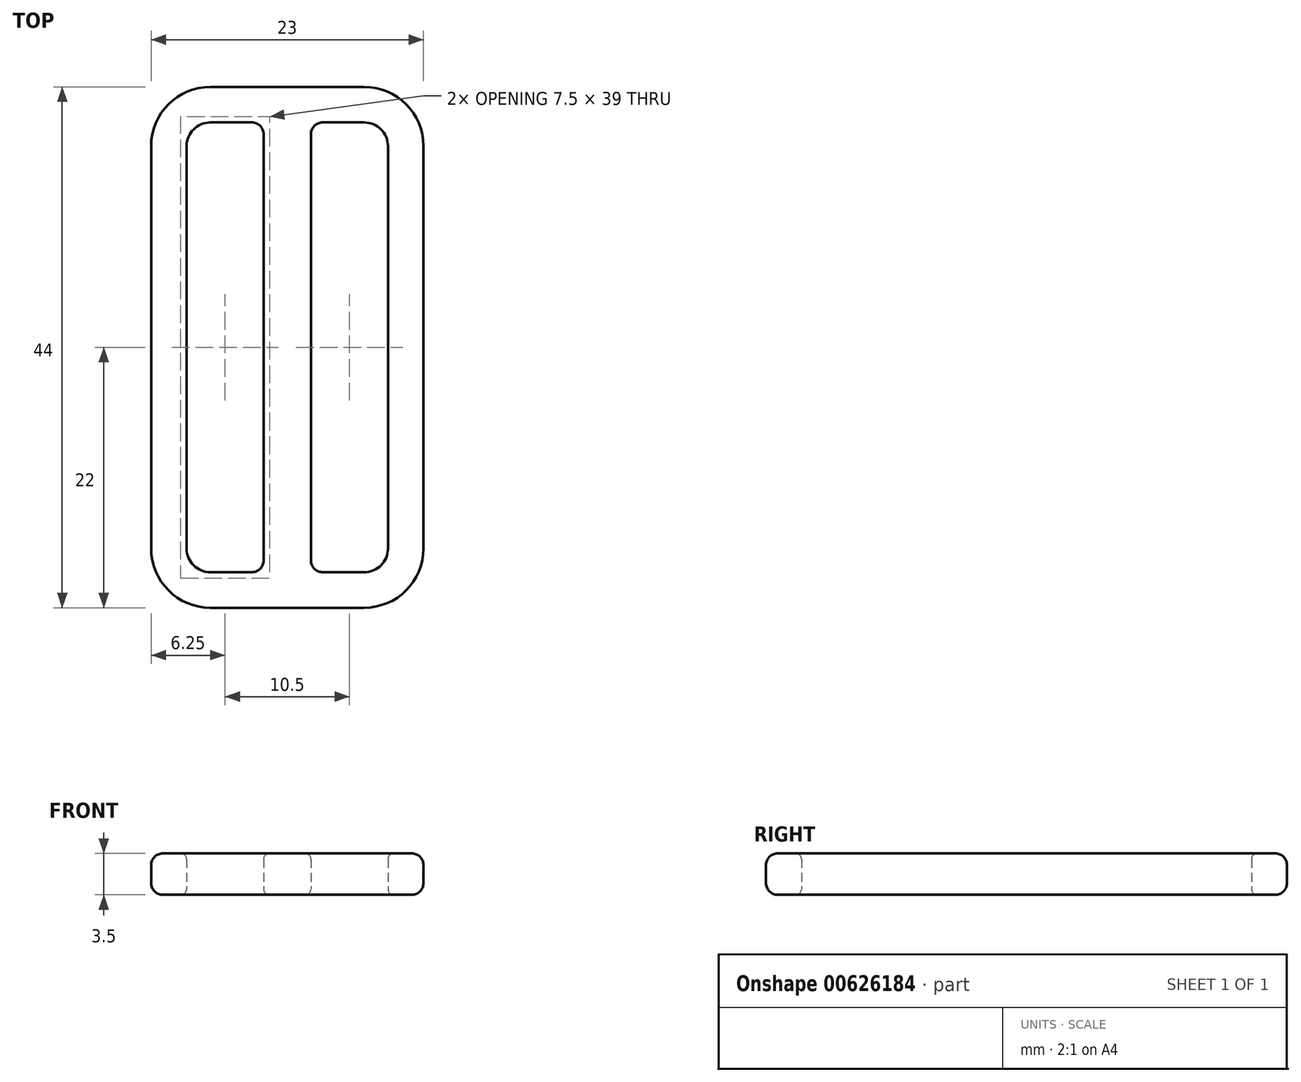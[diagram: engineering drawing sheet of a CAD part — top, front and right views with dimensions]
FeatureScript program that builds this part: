
annotation { "Feature Type Name" : "Feature", "Feature Type Description" : "" }
export const myFeature = defineFeature(function(context is Context, id is Id, definition is map)
    precondition{}
    {
        {
            var Q0;
            Q0=qCreatedBy(makeId("Top.planeOp"),FACE);
            var sketch = newSketch(context, id + "F0", { "sketchPlane" : qUnion([Q0])});
            skLineSegment(sketch, "E0.bottom", {"start": v(-8.5, 19) * mm, "end": v(-2, 19) * mm});
            skLineSegment(sketch, "E0.top", {"start": v(-8.5, -19) * mm, "end": v(-2, -19) * mm});
            skLineSegment(sketch, "E0.left", {"start": v(-8.5, 19) * mm, "end": v(-8.5, -19) * mm});
            skLineSegment(sketch, "E0.right", {"start": v(-2, 19) * mm, "end": v(-2, -19) * mm});
            skLineSegment(sketch, "E1.bottom", {"start": v(2, 19) * mm, "end": v(8.5, 19) * mm});
            skLineSegment(sketch, "E1.top", {"start": v(2, -19) * mm, "end": v(8.5, -19) * mm});
            skLineSegment(sketch, "E1.left", {"start": v(8.5, 19) * mm, "end": v(8.5, -19) * mm});
            skLineSegment(sketch, "E1.right", {"start": v(2, 19) * mm, "end": v(2, -19) * mm});
            skLineSegment(sketch, "E2", {"start": v(-2, 0) * mm, "end": v(2, 0) * mm, "construction": true});
            skPoint(sketch, "E3", {"position": v(0, 0) * mm});
            skLineSegment(sketch, "E4.bottom", {"start": v(-6.5, 22) * mm, "end": v(6.5, 22) * mm});
            skLineSegment(sketch, "E4.top", {"start": v(-6.5, -22) * mm, "end": v(6.5, -22) * mm});
            skLineSegment(sketch, "E4.left", {"start": v(-11.5, 17) * mm, "end": v(-11.5, -17) * mm});
            skLineSegment(sketch, "E4.right", {"start": v(11.5, 17) * mm, "end": v(11.5, -17) * mm});
            skPoint(sketch, "E5.visualSharp", {"position": v(-11.5, 22) * mm});
            skArc(sketch, "E5.filletArc", {"start": v(-6.5, 22) * mm, "mid": v(-10.04, 20.54) * mm, "end": v(-11.5, 17) * mm});
            skPoint(sketch, "E6.visualSharp", {"position": v(11.5, 22) * mm});
            skArc(sketch, "E6.filletArc", {"start": v(11.5, 17) * mm, "mid": v(10.04, 20.54) * mm, "end": v(6.5, 22) * mm});
            skPoint(sketch, "E7.visualSharp", {"position": v(11.5, -22) * mm});
            skArc(sketch, "E7.filletArc", {"start": v(6.5, -22) * mm, "mid": v(10.04, -20.54) * mm, "end": v(11.5, -17) * mm});
            skPoint(sketch, "E8.visualSharp", {"position": v(-11.5, -22) * mm});
            skArc(sketch, "E8.filletArc", {"start": v(-11.5, -17) * mm, "mid": v(-10.04, -20.54) * mm, "end": v(-6.5, -22) * mm});
            skSolve(sketch);
        }
        {
            var Q0;
            Q0=makeQuery(id+"F0.imprint","IMPRINT",FACE,{"disambiguationData":[TD([[makeQuery(id+"F0.imprint","IMPRINT",EDGE,{"derivedFrom":sQuery(id+"F0.wireOp",EDGE,"E0.bottom")}),1.0]])]});
            extrude(context, id + "F1", {"entities" : qUnion([Q0]), "depth" : 3.5 * mm, "offsetDistance" : 25 * mm});
        }
        {
            var Q0;
            Q0=makeQuery(id+"F1.opExtrude","SWEPT_EDGE",EDGE,{"disambiguationData":[OSD([sQuery(id+"F0.wireOp",EDGE,"E0.bottom"),sQuery(id+"F0.wireOp",EDGE,"E0.left")])]});
            var Q1;
            Q1=makeQuery(id+"F1.opExtrude","SWEPT_EDGE",EDGE,{"disambiguationData":[OSD([sQuery(id+"F0.wireOp",EDGE,"E1.top"),sQuery(id+"F0.wireOp",EDGE,"E1.left")])]});
            var Q2;
            Q2=makeQuery(id+"F1.opExtrude","SWEPT_EDGE",EDGE,{"disambiguationData":[OSD([sQuery(id+"F0.wireOp",EDGE,"E1.bottom"),sQuery(id+"F0.wireOp",EDGE,"E1.left")])]});
            var Q3;
            Q3=makeQuery(id+"F1.opExtrude","SWEPT_EDGE",EDGE,{"disambiguationData":[OSD([sQuery(id+"F0.wireOp",EDGE,"E0.top"),sQuery(id+"F0.wireOp",EDGE,"E0.left")])]});
            fillet(context, id + "F2", {"entities" : qUnion([Q0, Q1, Q2, Q3]), "radius" : 2 * mm, "tangentPropagation" : true, "allowEdgeOverflow" : false});
        }
        {
            var Q0;
            Q0=makeQuery(id+"F1.opExtrude","SWEPT_EDGE",EDGE,{"disambiguationData":[OSD([sQuery(id+"F0.wireOp",EDGE,"E1.bottom"),sQuery(id+"F0.wireOp",EDGE,"E1.right")])]});
            var Q1;
            Q1=makeQuery(id+"F1.opExtrude","SWEPT_EDGE",EDGE,{"disambiguationData":[OSD([sQuery(id+"F0.wireOp",EDGE,"E0.bottom"),sQuery(id+"F0.wireOp",EDGE,"E0.right")])]});
            var Q2;
            Q2=makeQuery(id+"F1.opExtrude","SWEPT_EDGE",EDGE,{"disambiguationData":[OSD([sQuery(id+"F0.wireOp",EDGE,"E0.top"),sQuery(id+"F0.wireOp",EDGE,"E0.right")])]});
            var Q3;
            Q3=makeQuery(id+"F1.opExtrude","SWEPT_EDGE",EDGE,{"disambiguationData":[OSD([sQuery(id+"F0.wireOp",EDGE,"E1.top"),sQuery(id+"F0.wireOp",EDGE,"E1.right")])]});
            fillet(context, id + "F3", {"entities" : qUnion([Q0, Q1, Q2, Q3]), "radius" : 1 * mm, "tangentPropagation" : true, "allowEdgeOverflow" : false});
        }
        {
            var Q0;
            Q0=makeQuery(id+"F1.opExtrude","CAP_EDGE",EDGE,{"disambiguationData":[OSD([sQuery(id+"F0.wireOp",EDGE,"E4.left")])],"isStart":false});
            var Q1;
            {var subQ0=sQuery(id+"F0.wireOp",EDGE,"E1.right");var subQ1=sQuery(id+"F0.wireOp",EDGE,"E1.bottom");Q1=makeQuery(id+"F2.opFillet","BLEND_EDGE",EDGE,{"blendedFrom":[makeQuery(id+"F1.opExtrude","SWEPT_EDGE",EDGE,{"disambiguationData":[OSD([subQ1,subQ0])]}),makeQuery(id+"F1.opExtrude","CAP_FACE",FACE,{"disambiguationData":[OSD([sQuery(id+"F0.wireOp",EDGE,"E0.bottom"),sQuery(id+"F0.wireOp",EDGE,"E0.top"),sQuery(id+"F0.wireOp",EDGE,"E0.left"),sQuery(id+"F0.wireOp",EDGE,"E0.right"),subQ1,sQuery(id+"F0.wireOp",EDGE,"E1.top"),sQuery(id+"F0.wireOp",EDGE,"E1.left"),subQ0,sQuery(id+"F0.wireOp",EDGE,"E4.bottom"),sQuery(id+"F0.wireOp",EDGE,"E4.top"),sQuery(id+"F0.wireOp",EDGE,"E4.left"),sQuery(id+"F0.wireOp",EDGE,"E4.right"),sQuery(id+"F0.wireOp",EDGE,"E5.filletArc"),sQuery(id+"F0.wireOp",EDGE,"E6.filletArc"),sQuery(id+"F0.wireOp",EDGE,"E7.filletArc"),sQuery(id+"F0.wireOp",EDGE,"E8.filletArc")])],"isStart":true})],"blendedInto":[makeQuery(id+"F1.opExtrude","CAP_FACE",FACE,{"disambiguationData":[OSD([sQuery(id+"F0.wireOp",EDGE,"E0.bottom"),sQuery(id+"F0.wireOp",EDGE,"E0.top"),sQuery(id+"F0.wireOp",EDGE,"E0.left"),sQuery(id+"F0.wireOp",EDGE,"E0.right"),subQ1,sQuery(id+"F0.wireOp",EDGE,"E1.top"),sQuery(id+"F0.wireOp",EDGE,"E1.left"),subQ0,sQuery(id+"F0.wireOp",EDGE,"E4.bottom"),sQuery(id+"F0.wireOp",EDGE,"E4.top"),sQuery(id+"F0.wireOp",EDGE,"E4.left"),sQuery(id+"F0.wireOp",EDGE,"E4.right"),sQuery(id+"F0.wireOp",EDGE,"E5.filletArc"),sQuery(id+"F0.wireOp",EDGE,"E6.filletArc"),sQuery(id+"F0.wireOp",EDGE,"E7.filletArc"),sQuery(id+"F0.wireOp",EDGE,"E8.filletArc")])],"isStart":true})]});}
            var Q2;
            Q2=makeQuery(id+"F1.opExtrude","CAP_EDGE",EDGE,{"disambiguationData":[OSD([sQuery(id+"F0.wireOp",EDGE,"E4.right")])],"isStart":true});
            fillet(context, id + "F4", {"entities" : qUnion([Q0, Q1, Q2]), "radius" : 1 * mm, "tangentPropagation" : true, "allowEdgeOverflow" : false});
        }
        {
            var Q0;
            Q0=makeQuery(id+"F1.opExtrude","CAP_EDGE",EDGE,{"disambiguationData":[OSD([sQuery(id+"F0.wireOp",EDGE,"E1.top")])],"isStart":false});
            var Q1;
            {var subQ0=sQuery(id+"F0.wireOp",EDGE,"E0.right");var subQ1=sQuery(id+"F0.wireOp",EDGE,"E0.top");Q1=makeQuery(id+"F3.opFillet","BLEND_EDGE",EDGE,{"blendedFrom":[makeQuery(id+"F1.opExtrude","SWEPT_EDGE",EDGE,{"disambiguationData":[OSD([subQ1,subQ0])]}),makeQuery(id+"F1.opExtrude","CAP_FACE",FACE,{"disambiguationData":[OSD([sQuery(id+"F0.wireOp",EDGE,"E0.bottom"),subQ1,sQuery(id+"F0.wireOp",EDGE,"E0.left"),subQ0,sQuery(id+"F0.wireOp",EDGE,"E1.bottom"),sQuery(id+"F0.wireOp",EDGE,"E1.top"),sQuery(id+"F0.wireOp",EDGE,"E1.left"),sQuery(id+"F0.wireOp",EDGE,"E1.right"),sQuery(id+"F0.wireOp",EDGE,"E4.bottom"),sQuery(id+"F0.wireOp",EDGE,"E4.top"),sQuery(id+"F0.wireOp",EDGE,"E4.left"),sQuery(id+"F0.wireOp",EDGE,"E4.right"),sQuery(id+"F0.wireOp",EDGE,"E5.filletArc"),sQuery(id+"F0.wireOp",EDGE,"E6.filletArc"),sQuery(id+"F0.wireOp",EDGE,"E7.filletArc"),sQuery(id+"F0.wireOp",EDGE,"E8.filletArc")])],"isStart":false})],"blendedInto":[makeQuery(id+"F1.opExtrude","CAP_FACE",FACE,{"disambiguationData":[OSD([sQuery(id+"F0.wireOp",EDGE,"E0.bottom"),subQ1,sQuery(id+"F0.wireOp",EDGE,"E0.left"),subQ0,sQuery(id+"F0.wireOp",EDGE,"E1.bottom"),sQuery(id+"F0.wireOp",EDGE,"E1.top"),sQuery(id+"F0.wireOp",EDGE,"E1.left"),sQuery(id+"F0.wireOp",EDGE,"E1.right"),sQuery(id+"F0.wireOp",EDGE,"E4.bottom"),sQuery(id+"F0.wireOp",EDGE,"E4.top"),sQuery(id+"F0.wireOp",EDGE,"E4.left"),sQuery(id+"F0.wireOp",EDGE,"E4.right"),sQuery(id+"F0.wireOp",EDGE,"E5.filletArc"),sQuery(id+"F0.wireOp",EDGE,"E6.filletArc"),sQuery(id+"F0.wireOp",EDGE,"E7.filletArc"),sQuery(id+"F0.wireOp",EDGE,"E8.filletArc")])],"isStart":false})]});}
            var Q2;
            Q2=makeQuery(id+"F1.opExtrude","CAP_EDGE",EDGE,{"disambiguationData":[OSD([sQuery(id+"F0.wireOp",EDGE,"E0.top")])],"isStart":true});
            var Q3;
            Q3=makeQuery(id+"F1.opExtrude","CAP_EDGE",EDGE,{"disambiguationData":[OSD([sQuery(id+"F0.wireOp",EDGE,"E1.top")])],"isStart":true});
            fillet(context, id + "F5", {"entities" : qUnion([Q0, Q1, Q2, Q3]), "radius" : .5 * mm, "tangentPropagation" : true, "allowEdgeOverflow" : false});
        }
    });
